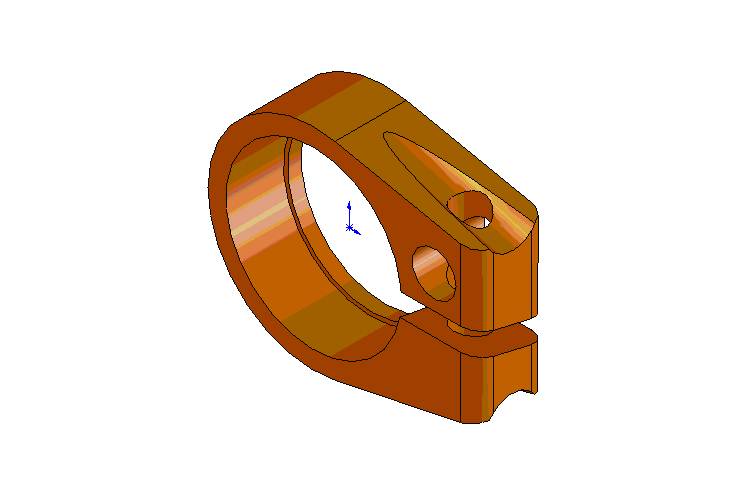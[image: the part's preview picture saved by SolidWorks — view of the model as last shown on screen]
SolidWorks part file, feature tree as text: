
SOLIDWORKS PART (.sldprt)
format: sldprt  version: not decoded by parser v0  size: 384,512 bytes
history: native  units: mm
features: sketch x7, cut_extrude x5, plane x3, material x1, extrude x1, fillet x1, cut_revolve x1, mirror x1 (+10 scaffold rows collapsed)
feature tree (30):
  scaffold x10  (default folders/planes/origin — collapsed)
  material  "Matériau <non spécifié>"
  plane  "Plan de face"
  plane  "Plan de dessus"
  plane  "Plan de droite"
  sketch  "Esquisse1"  dims[c1.D1=38.5mm c1.D3=38.5mm c1.D4=30.5mm c1.D2=27.0mm c2.D3=49.0mm]
  extrude  "Extrusion1"  Depth=13mm
  sketch  "Esquisse2"  dims[D1=32.0mm]
  cut_extrude  "Enlèv. mat.-Extru.1"  Depth=10.5mm
  sketch  "Esquisse3"  dims[c1.D1=4.0mm c1.D2=7.5mm c1.D3=~20.785322mm c2.D3=13.0deg]
  cut_extrude  "Enlèv. mat.-Extru.2"  [1 undecoded]
  sketch  "Esquisse4"  dims[c1.D1=8.0mm c1.D2=41.0mm c1.D3=7.0mm c2.D2=22.0mm]
  cut_extrude  "Enlèv. mat.-Extru.3"  [1 undecoded]
  fillet  "Congé2"  Radius=3mm
  sketch  "Esquisse5"  dims[D1=6.0mm]
  cut_extrude  "Enlèv. mat.-Extru.4"  [1 undecoded]
  sketch  "Esquisse6"  dims[D1=9.0mm]
  cut_extrude  "Enlèv. mat.-Extru.5"  [1 undecoded]
  sketch  "Esquisse7"  dims[c1.D1=~20.747599mm c2.D1=7.0deg c3.D1=~34.790725mm c4.D1=17.0deg c4.D2=10.0mm c4.D3=11.2mm]
  cut_revolve  "Enlèvement de matière-Révolution1"  Angle=360deg
  mirror  "Symétrie1"
decode coverage: 11 of 16 modeling features carry decoded parameters
note: ~ marks probable driven/reference dimensions
note: 4 parameter values undecoded
summary: no parameter record found for 4 features
note: suppression state not decoded; provenance and decode notes live in map.json
